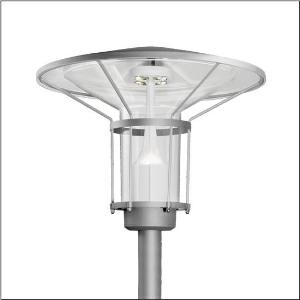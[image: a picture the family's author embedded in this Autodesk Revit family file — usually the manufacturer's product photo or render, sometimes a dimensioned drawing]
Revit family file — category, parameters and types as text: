
# Revit family: laterne_classic_iq___st1_2a_5xa5245ef14h000022_520b
name_source: partatom
category: Lighting Fixtures
units: mm (PartAtom-declared; Revit-internal decimal feet)

## family parameters
Cut with Voids When Loaded = No
Host = Face
Light Source = No
Part Type = Normal
Room Calculation Point = No
Round Connector Dimension = Use Diameter
Shared = No

## types (1)
- --- (1 x LED, 1380 lm, 10.5 W, 3000K)
    Apparent Load = 11 VA
    CIE Flux Codes = 21 60 93 97 100
    Color Rendering = 70
    Color Temperature = 3000K
    Default Elevation = 1800 mm
    Description = Lantern Classic iQ, mast luminaire, Module 540 iQ-SR, primary light control with 3 zone facetted reflector, of plastic, silver coated, highly specular, structured, primary optical cover: cover, of PMMA, transparent, light distribution: ST1.2a, light emission: direct distribution, primary light characteristic: asymmetric, installation type: post-top, LED, High Power LED, rated luminous flux: 1.380lm, luminous efficacy: 131lm/W, light colour: 730, colour temperature: 3000K, control gear: ECG iQ, control: Street-Remote, Auto-Match, Temp-Guard, Lumen-Switch, Night-Set, Smart-Wire, Light-Fading, Desk-Remote (wireless, voltage-free reading and setting of iQ features in the workshop via application-optimized NFC function/RFID function), optimised constant luminous flux control (CLO 2.0), pre-setting: logarithmic dimming characteristic, mains connection: 230..240V, AC, 50/60Hz, connection cable pre-assembled, cable length: 5,5m, wiring characteristics: H07RN-F, start of lifetime: 11W, end of service life: 11W, reduction: 5W, luminaire housing, upper part, of glass-fibre reinforced polyester, coated, Siteco® metallic grey (DB 702S), diameter: 750mm, height: 596mm, spigot size: d x l = 76 x 70mm (post-top) | with reducer (optional accessory) 60 x 70mm, post-top mast mounting element, of diecast aluminium, coated, Siteco® metallic grey (DB 702S), Module 540 iQ-SR, traffic white (RAL 9016), equipment: standard, protection rating (complete): IP65, insulation class (complete): insulation class II (safety insulation), certification: CE, ENEC, VDE, packaging unit: 1 piece

Light Distribution: ST1.2a
    Height = 596 mm
    Lamp = 1 x LED
    Lamp Light Flux = 1380 lm
    Lamp Power = 10.5 W
    Lamp count = 1
    Length = 750 mm
    Luminous efficacy = 131 lm/W
    Manufacturer = Siteco
    ModVariant = No
    Model = 5XA5245EF14H000022
    Number of Poles = 1
    OnlyDefault = Yes
    Power Factor = 1
    Product Name = Laterne Classic iQ | ST1.2a
    Product group = mast luminaire | pylon top
    ProductGroupID = 6100
    Protection Class = Protection class II
    Protection Degree = IP 65
    RLX_Detail_Level = 1
    RLX_Emergency_Light_Flux = 0 lm
    RLX_Emergency_Type = 0
    RLX_Emergency_Type_DB = No
    RlxData = <blob elided: 64149 chars, md5=cb94e747>
    Socket = socket
    Standby Power = 0 W
    System Light Flux = 1380 lm
    System Power = 11 W
    Type Comments = factory setting: luminous flux: 100 % | dim-lin: 254 | 419 mA
    Type Image = l_1006052.jpg
    URL = http://relux.com
    VarID = @adj_130669
    Voltage = 0 V
    Weight = 0.00 kg
    Width = 0 mm  [stored 0 ft]

note: [stored X ft] marks values corroborated as IEEE doubles in the binary element streams (Revit-internal decimal feet)

## geometry (parser evidence)
native form markers: Blend x4, Sweep x9
no freeform markers — native parametric forms only
